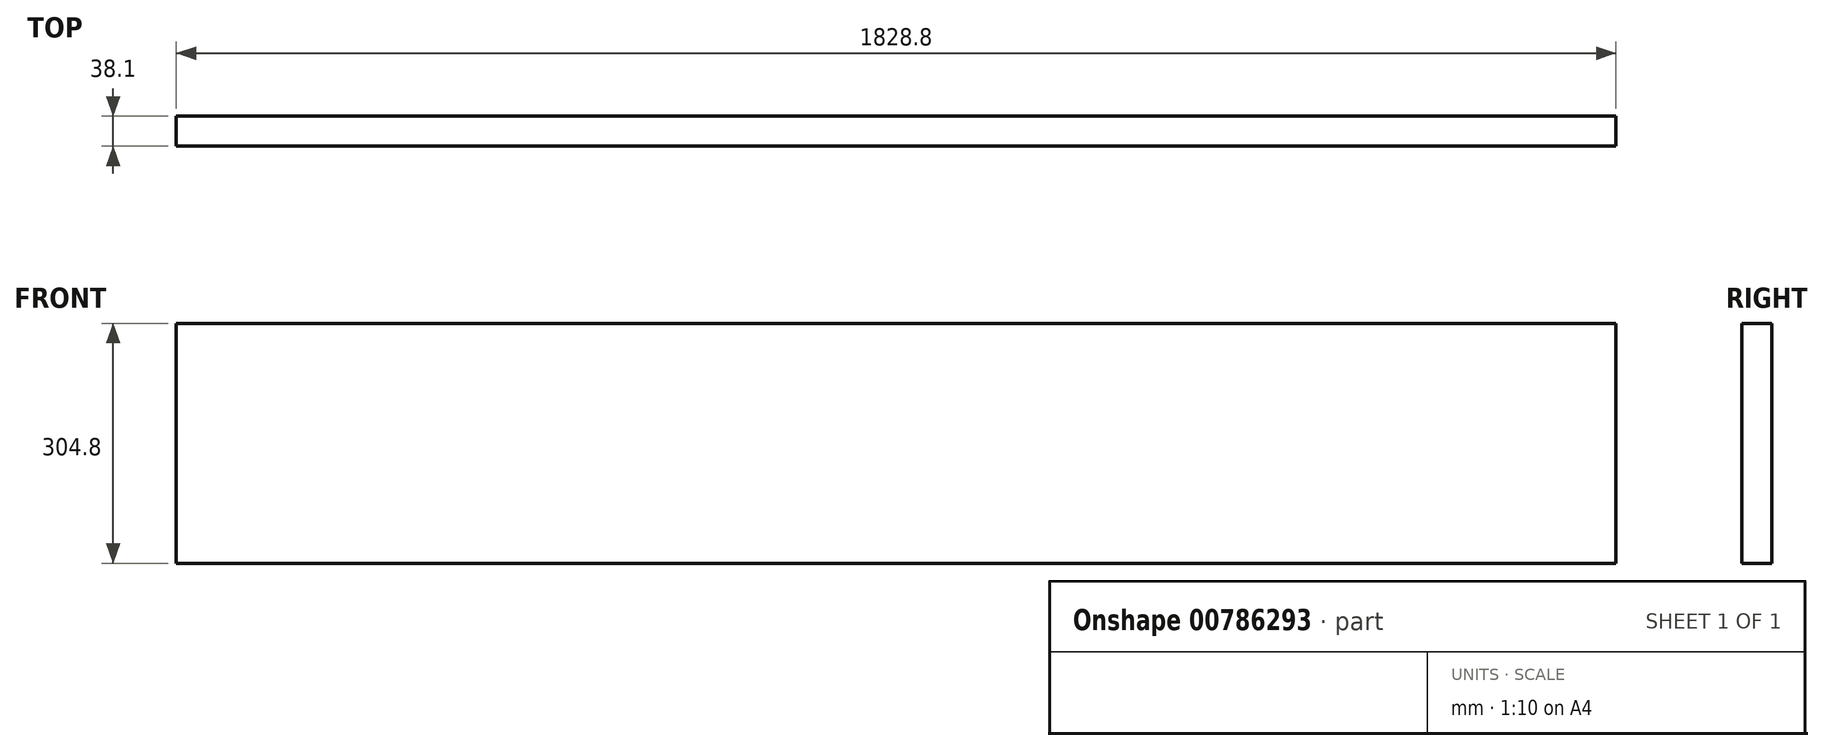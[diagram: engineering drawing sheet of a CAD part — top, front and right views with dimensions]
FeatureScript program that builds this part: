
annotation { "Feature Type Name" : "Feature", "Feature Type Description" : "" }
export const myFeature = defineFeature(function(context is Context, id is Id, definition is map)
    precondition{}
    {
        {
            var Q0;
            Q0=qCreatedBy(makeId("Front.planeOp"),FACE);
            var sketch = newSketch(context, id + "F0", { "sketchPlane" : qUnion([Q0])});
            skLineSegment(sketch, "E0.bottom", {"start": v(-914.4, 152.4) * mm, "end": v(914.4, 152.4) * mm});
            skLineSegment(sketch, "E0.top", {"start": v(-914.4, -152.4) * mm, "end": v(914.4, -152.4) * mm});
            skLineSegment(sketch, "E0.left", {"start": v(-914.4, 152.4) * mm, "end": v(-914.4, -152.4) * mm});
            skLineSegment(sketch, "E0.right", {"start": v(914.4, 152.4) * mm, "end": v(914.4, -152.4) * mm});
            skPoint(sketch, "E0.middle", {"position": v(0, 0) * mm});
            skSolve(sketch);
        }
        {
            var Q0;
            Q0=makeQuery(id+"F0.imprint","IMPRINT",FACE,{"disambiguationData":[TD([[makeQuery(id+"F0.imprint","IMPRINT",EDGE,{"derivedFrom":sQuery(id+"F0.wireOp",EDGE,"E0.bottom")}),-1.0]])]});
            extrude(context, id + "F1", {"entities" : qUnion([Q0]), "endBound" : BoundingType.SYMMETRIC, "depth" : 38.1 * mm, "offsetDistance" : 25.4 * mm});
        }
    });
